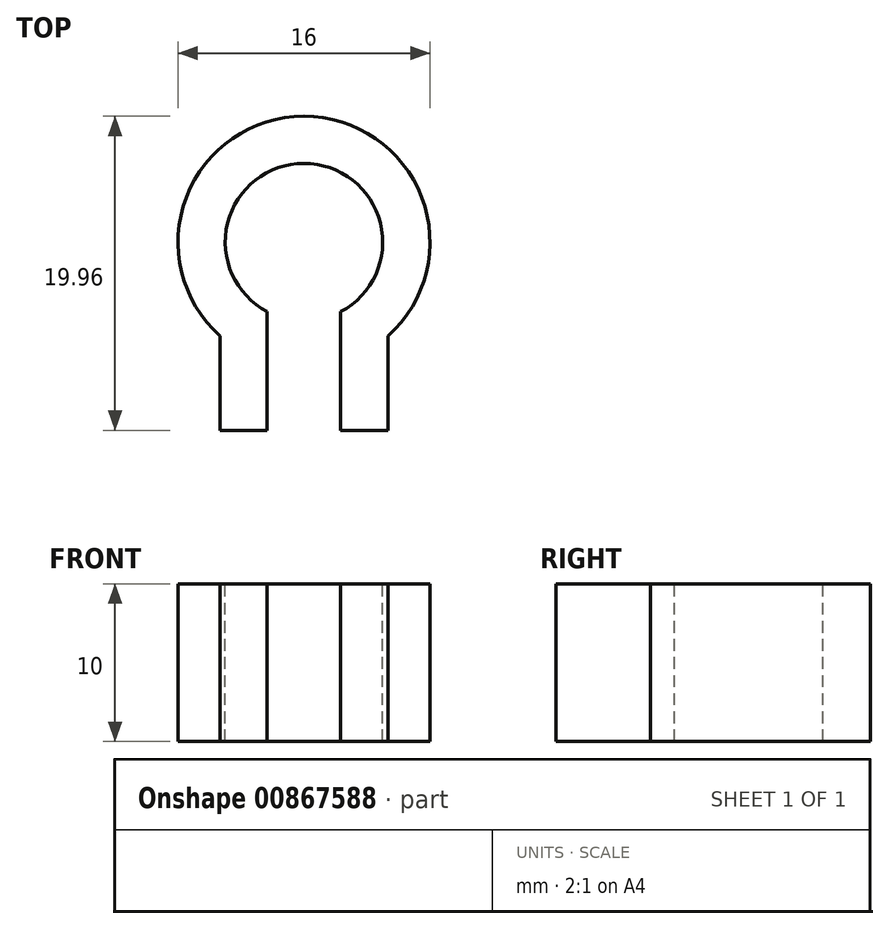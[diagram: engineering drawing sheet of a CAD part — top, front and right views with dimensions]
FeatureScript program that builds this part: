
annotation { "Feature Type Name" : "Feature", "Feature Type Description" : "" }
export const myFeature = defineFeature(function(context is Context, id is Id, definition is map)
    precondition{}
    {
        {
            var Q0;
            Q0=qCreatedBy(makeId("Top.planeOp"),FACE);
            var sketch = newSketch(context, id + "F0", { "sketchPlane" : qUnion([Q0])});
            skArc(sketch, "E0", {"start": v(5.33, -5.96) * mm, "mid": v(0, 8) * mm, "end": v(-5.33, -5.96) * mm});
            skLineSegment(sketch, "E1", {"start": v(0, 27) * mm, "end": v(0, -32.85) * mm, "construction": true});
            skLineSegment(sketch, "E2", {"start": v(-5.33, -5.96) * mm, "end": v(-5.33, -11.96) * mm});
            skLineSegment(sketch, "E3", {"start": v(-5.33, -11.96) * mm, "end": v(0, -11.96) * mm});
            skLineSegment(sketch, "E4.MirrorCS", {"start": v(5.33, -5.96) * mm, "end": v(5.33, -11.96) * mm});
            skLineSegment(sketch, "E5.MirrorCS", {"start": v(5.33, -11.96) * mm, "end": v(0, -11.96) * mm});
            skSolve(sketch);
        }
        {
            var Q0;
            Q0 = qSketchRegion(id + "F0", true);
            extrude(context, id + "F1", {"entities" : qUnion([Q0]), "endBound" : BoundingType.SYMMETRIC, "depth" : 10 * mm, "offsetDistance" : 25 * mm});
        }
        {
            var Q0;
            Q0=makeQuery(id+"F1.opExtrude","CAP_FACE",FACE,{"disambiguationData":[OSD([sQuery(id+"F0.wireOp",EDGE,"E0"),sQuery(id+"F0.wireOp",EDGE,"E2"),sQuery(id+"F0.wireOp",EDGE,"E3"),sQuery(id+"F0.wireOp",EDGE,"E4.MirrorCS"),sQuery(id+"F0.wireOp",EDGE,"E5.MirrorCS")])],"isStart":false});
            var sketch = newSketch(context, id + "F2", { "sketchPlane" : qUnion([Q0])});
            skLineSegment(sketch, "E6.0", {"start": v(-2.33, -4.42) * mm, "end": v(-2.33, -26.18) * mm});
            skArc(sketch, "E6.1", {"start": v(2.33, -4.42) * mm, "mid": v(0, 5) * mm, "end": v(-2.33, -4.42) * mm});
            skLineSegment(sketch, "E6.2", {"start": v(2.33, -4.42) * mm, "end": v(2.33, -26.18) * mm});
            skLineSegment(sketch, "E7", {"start": v(-2.33, -26.18) * mm, "end": v(2.33, -26.18) * mm});
            skSolve(sketch);
        }
        {
            var Q0;
            Q0 = qSketchRegion(id + "F2", true);
            extrude(context, id + "F3", {"entities" : qUnion([Q0]), "operationType" : NewBodyOperationType.REMOVE, "oppositeDirection" : true, "depth" : 10 * mm, "offsetDistance" : 25 * mm});
        }
    });
